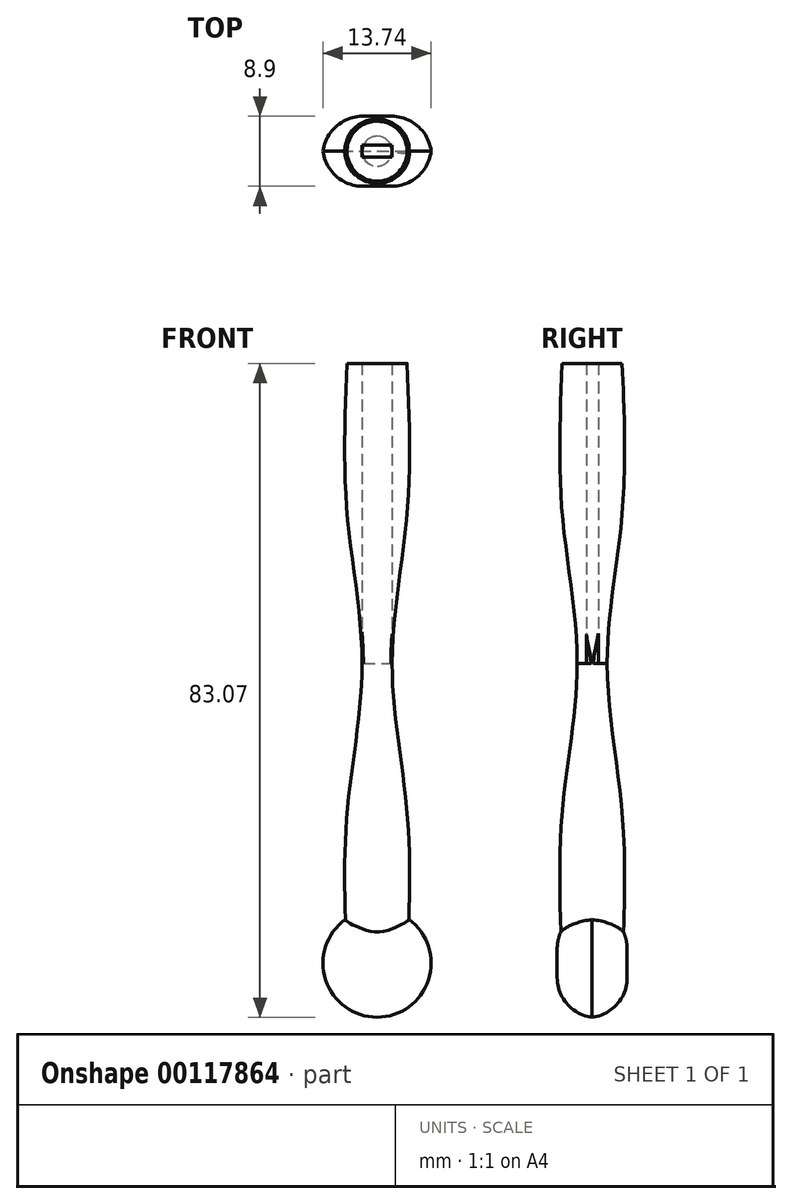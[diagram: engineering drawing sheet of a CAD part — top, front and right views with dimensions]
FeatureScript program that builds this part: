
annotation { "Feature Type Name" : "Feature", "Feature Type Description" : "" }
export const myFeature = defineFeature(function(context is Context, id is Id, definition is map)
    precondition{}
    {
        {
            var Q0;
            Q0=qCreatedBy(makeId("Front.planeOp"),FACE);
            var sketch = newSketch(context, id + "F0", { "sketchPlane" : qUnion([Q0])});
            skLineSegment(sketch, "E0", {"start": v(0, 0) * mm, "end": v(-1.9, 0) * mm});
            skLineSegment(sketch, "E1.MirrorCS", {"start": v(0, 0) * mm, "end": v(1.9, 0) * mm});
            skLineSegment(sketch, "E2", {"start": v(0, 0) * mm, "end": v(0, 38.1) * mm});
            skLineSegment(sketch, "E3.MirrorCS", {"start": v(0, 0) * mm, "end": v(0, -38.1) * mm});
            skLineSegment(sketch, "E4", {"start": v(0, 38.1) * mm, "end": v(-3.81, 38.1) * mm});
            skLineSegment(sketch, "E5.MirrorCS", {"start": v(0, 38.1) * mm, "end": v(3.81, 38.1) * mm});
            skLineSegment(sketch, "E6.MirrorCS", {"start": v(0, -38.1) * mm, "end": v(-3.81, -38.1) * mm});
            skLineSegment(sketch, "E7.MirrorCS", {"start": v(0, -38.1) * mm, "end": v(3.81, -38.1) * mm});
            skPoint(sketch, "E8.1.internal.snap0", {"position": v(0, 19.05) * mm});
            skPoint(sketch, "E8.1.internal.snap1", {"position": v(-1.9, 38.1) * mm});
            skPoint(sketch, "E8.3.internal.snap0", {"position": v(0, -19.05) * mm});
            skPoint(sketch, "E8.3.internal.snap1", {"position": v(-1.9, 38.1) * mm});
            skCircle(sketch, "E9", {"center": v(0, -38.1) * mm, "radius": 6.9 * mm});
            skLineSegment(sketch, "E10", {"start": v(0, -31.2) * mm, "end": v(0, -45) * mm});
            skFitSpline(sketch, "E11", {"points": [v(3.81, 38.1) * mm, v(3.81, 19.05) * mm, v(1.9, 0) * mm, v(3.81, -19.05) * mm, v(3.81, -38.1) * mm], "startDerivative": vector(3.26, -76.34) * mm, "endDerivative": vector(-3.26, -76.34) * mm});
            skFitSpline(sketch, "E12.MirrorCS", {"points": [v(-3.81, 38.1) * mm, v(-3.81, 19.05) * mm, v(-1.9, 0) * mm, v(-3.81, -19.05) * mm, v(-3.81, -38.1) * mm], "startDerivative": vector(-3.26, -76.34) * mm, "endDerivative": vector(3.26, -76.34) * mm});
            skSolve(sketch);
        }
        {
            var Q0;
            Q0=qCreatedBy(makeId("Top.planeOp"),FACE);
            var sketch = newSketch(context, id + "F1", { "sketchPlane" : qUnion([Q0])});
            skLineSegment(sketch, "E13", {"start": v(-1.91, 0.77) * mm, "end": v(1.9, 0.77) * mm});
            skLineSegment(sketch, "E14.MirrorCS", {"start": v(-1.91, -0.75) * mm, "end": v(1.9, -0.75) * mm});
            skLineSegment(sketch, "E15", {"start": v(-1.91, 0.77) * mm, "end": v(-1.91, -0.75) * mm});
            skLineSegment(sketch, "E16", {"start": v(1.9, 0.77) * mm, "end": v(1.9, -0.75) * mm});
            skSolve(sketch);
        }
        {
            var Q0;
            {var subQ0=sQuery(id+"F0.wireOp",EDGE,"E1.MirrorCS");Q0=makeQuery(id+"F0.imprint","IMPRINT",FACE,{"disambiguationData":[TD([[makeQuery(id+"F0.imprint","IMPRINT",EDGE,{"derivedFrom":subQ0}),1.0]])]});}
            var Q1;
            {var subQ0=sQuery(id+"F0.wireOp",EDGE,"E1.MirrorCS");Q1=makeQuery(id+"F0.imprint","IMPRINT",FACE,{"disambiguationData":[TD([[makeQuery(id+"F0.imprint","IMPRINT",EDGE,{"derivedFrom":subQ0}),-1.0]])]});}
            var Q2;
            Q2=sQuery(id+"F0.wireOp",EDGE,"E2");
            revolve(context, id + "F2", {"entities" : qUnion([Q0, Q1]), "axis" : qUnion([Q2]), "revolveType" : RevolveType.FULL});
        }
        {
            var Q0;
            {var subQ0=sQuery(id+"F0.wireOp",EDGE,"E6.MirrorCS");Q0=makeQuery(id+"F0.imprint","IMPRINT",FACE,{"disambiguationData":[TD([[makeQuery(id+"F0.imprint","IMPRINT",EDGE,{"derivedFrom":subQ0}),1.0]])]});}
            var Q1;
            {var subQ0=sQuery(id+"F0.wireOp",EDGE,"E6.MirrorCS");Q1=makeQuery(id+"F0.imprint","IMPRINT",FACE,{"disambiguationData":[TD([[makeQuery(id+"F0.imprint","IMPRINT",EDGE,{"derivedFrom":subQ0}),-1.0]])]});}
            var Q2;
            {var subQ0=sQuery(id+"F0.wireOp",EDGE,"E7.MirrorCS");Q2=makeQuery(id+"F0.imprint","IMPRINT",FACE,{"disambiguationData":[TD([[makeQuery(id+"F0.imprint","IMPRINT",EDGE,{"derivedFrom":subQ0}),-1.0]])]});}
            var Q3;
            {var subQ0=sQuery(id+"F0.wireOp",EDGE,"E7.MirrorCS");Q3=makeQuery(id+"F0.imprint","IMPRINT",FACE,{"disambiguationData":[TD([[makeQuery(id+"F0.imprint","IMPRINT",EDGE,{"derivedFrom":subQ0}),1.0]])]});}
            extrude(context, id + "F3", {"entities" : qUnion([Q0, Q1, Q2, Q3]), "operationType" : NewBodyOperationType.ADD, "endBound" : BoundingType.SYMMETRIC, "depth" : 8.9 * mm});
        }
        {
            var Q0;
            Q0=makeQuery(id+"F3.opExtrude","CAP_EDGE",EDGE,{"disambiguationData":[OSD([sQuery(id+"F0.wireOp",EDGE,"E9")])],"isStart":true});
            var Q1;
            Q1=makeQuery(id+"F3.opExtrude","CAP_EDGE",EDGE,{"disambiguationData":[OSD([sQuery(id+"F0.wireOp",EDGE,"E9")])],"isStart":false});
            fillet(context, id + "F4", {"entities" : qUnion([Q0, Q1]), "radius" : 5.08 * mm, "tangentPropagation" : true, "allowEdgeOverflow" : false});
        }
        {
            var Q0;
            Q0 = qSketchRegion(id + "F1", true);
            extrude(context, id + "F5", {"entities" : qUnion([Q0]), "operationType" : NewBodyOperationType.REMOVE, "depth" : 52.95 * mm});
        }
    });
